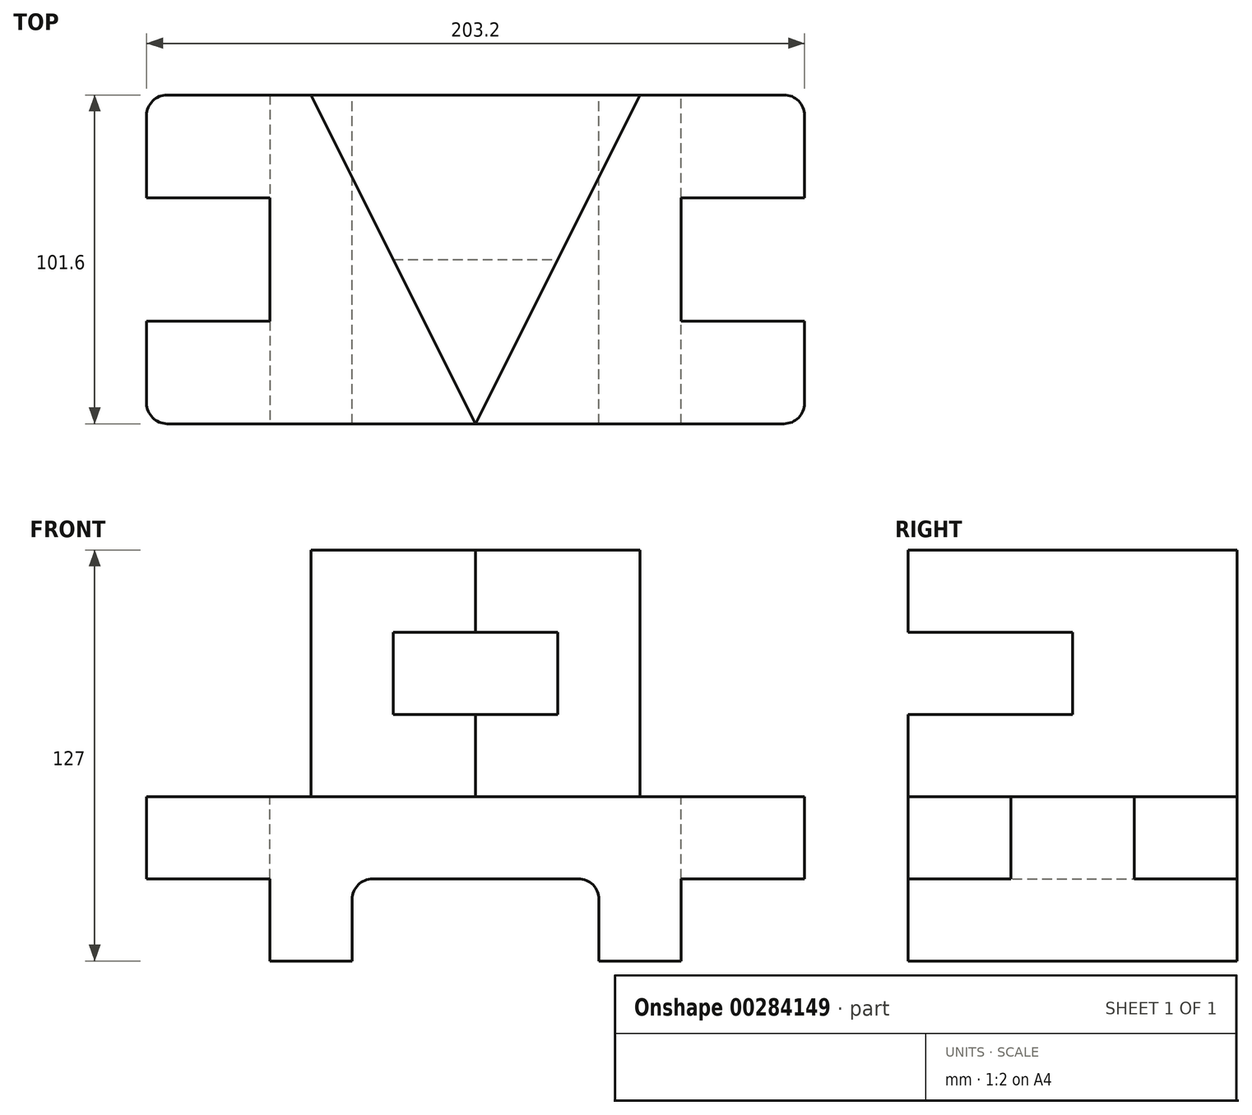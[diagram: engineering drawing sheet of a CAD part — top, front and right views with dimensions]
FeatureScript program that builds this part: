
annotation { "Feature Type Name" : "Feature", "Feature Type Description" : "" }
export const myFeature = defineFeature(function(context is Context, id is Id, definition is map)
    precondition{}
    {
        {
            var Q0;
            Q0=qCreatedBy(makeId("Top.planeOp"),FACE);
            var sketch = newSketch(context, id + "F0", { "sketchPlane" : qUnion([Q0])});
            skLineSegment(sketch, "E0", {"start": v(-63.5, 0) * mm, "end": v(63.5, 0) * mm, "construction": true});
            skLineSegment(sketch, "E1", {"start": v(-63.5, 19.05) * mm, "end": v(-63.5, -19.05) * mm});
            skLineSegment(sketch, "E2", {"start": v(-63.5, -19.05) * mm, "end": v(-101.6, -19.05) * mm});
            skLineSegment(sketch, "E3", {"start": v(-101.6, -19.05) * mm, "end": v(-101.6, -50.8) * mm});
            skLineSegment(sketch, "E4", {"start": v(-101.6, -50.8) * mm, "end": v(101.6, -50.8) * mm});
            skLineSegment(sketch, "E5", {"start": v(101.6, -50.8) * mm, "end": v(101.6, -19.05) * mm});
            skLineSegment(sketch, "E6", {"start": v(101.6, -19.05) * mm, "end": v(63.5, -19.05) * mm});
            skLineSegment(sketch, "E7", {"start": v(63.5, -19.05) * mm, "end": v(63.5, 19.05) * mm});
            skLineSegment(sketch, "E8", {"start": v(63.5, 19.05) * mm, "end": v(101.6, 19.05) * mm});
            skLineSegment(sketch, "E9", {"start": v(101.6, 19.05) * mm, "end": v(101.6, 50.8) * mm});
            skLineSegment(sketch, "E10", {"start": v(101.6, 50.8) * mm, "end": v(-101.6, 50.8) * mm});
            skLineSegment(sketch, "E11", {"start": v(-101.6, 50.8) * mm, "end": v(-101.6, 19.05) * mm});
            skLineSegment(sketch, "E12", {"start": v(-101.6, 19.05) * mm, "end": v(-63.5, 19.05) * mm});
            skSolve(sketch);
        }
        {
            var Q0;
            Q0=makeQuery(id+"F0.imprint","IMPRINT",FACE,{"disambiguationData":[TD([[makeQuery(id+"F0.imprint","IMPRINT",EDGE,{"derivedFrom":sQuery(id+"F0.wireOp",EDGE,"E1")}),1.0]])]});
            extrude(context, id + "F1", {"entities" : qUnion([Q0]), "oppositeDirection" : true, "depth" : 25.4 * mm});
        }
        {
            var Q0;
            Q0=makeQuery(id+"F1.opExtrude","SWEPT_EDGE",EDGE,{"disambiguationData":[OSD([sQuery(id+"F0.wireOp",EDGE,"E3"),sQuery(id+"F0.wireOp",EDGE,"E4")])]});
            var Q1;
            Q1=makeQuery(id+"F1.opExtrude","SWEPT_EDGE",EDGE,{"disambiguationData":[OSD([sQuery(id+"F0.wireOp",EDGE,"E4"),sQuery(id+"F0.wireOp",EDGE,"E5")])]});
            var Q2;
            Q2=makeQuery(id+"F1.opExtrude","SWEPT_EDGE",EDGE,{"disambiguationData":[OSD([sQuery(id+"F0.wireOp",EDGE,"E9"),sQuery(id+"F0.wireOp",EDGE,"E10")])]});
            var Q3;
            Q3=makeQuery(id+"F1.opExtrude","SWEPT_EDGE",EDGE,{"disambiguationData":[OSD([sQuery(id+"F0.wireOp",EDGE,"E10"),sQuery(id+"F0.wireOp",EDGE,"E11")])]});
            fillet(context, id + "F2", {"entities" : qUnion([Q0, Q1, Q2, Q3]), "radius" : 6.35 * mm, "tangentPropagation" : true, "allowEdgeOverflow" : false});
        }
        {
            var Q0;
            Q0=makeQuery(id+"F1.opExtrude","CAP_FACE",FACE,{"disambiguationData":[OSD([sQuery(id+"F0.wireOp",EDGE,"E1"),sQuery(id+"F0.wireOp",EDGE,"E2"),sQuery(id+"F0.wireOp",EDGE,"E3"),sQuery(id+"F0.wireOp",EDGE,"E4"),sQuery(id+"F0.wireOp",EDGE,"E5"),sQuery(id+"F0.wireOp",EDGE,"E6"),sQuery(id+"F0.wireOp",EDGE,"E7"),sQuery(id+"F0.wireOp",EDGE,"E8"),sQuery(id+"F0.wireOp",EDGE,"E9"),sQuery(id+"F0.wireOp",EDGE,"E10"),sQuery(id+"F0.wireOp",EDGE,"E11"),sQuery(id+"F0.wireOp",EDGE,"E12")])],"isStart":false});
            var sketch = newSketch(context, id + "F3", { "sketchPlane" : qUnion([Q0])});
            skLineSegment(sketch, "E13", {"start": v(63.5, 19.05) * mm, "end": v(63.5, 50.8) * mm});
            skLineSegment(sketch, "E14", {"start": v(63.5, 50.8) * mm, "end": v(38.1, 50.8) * mm});
            skLineSegment(sketch, "E15", {"start": v(38.1, 50.8) * mm, "end": v(38.1, -50.8) * mm});
            skLineSegment(sketch, "E16", {"start": v(38.1, -50.8) * mm, "end": v(63.5, -50.8) * mm});
            skLineSegment(sketch, "E17", {"start": v(63.5, -50.8) * mm, "end": v(63.5, -19.05) * mm});
            skLineSegment(sketch, "E18", {"start": v(63.5, -19.05) * mm, "end": v(63.5, 19.05) * mm});
            skLineSegment(sketch, "E19", {"start": v(-63.5, -50.8) * mm, "end": v(-63.5, -19.05) * mm});
            skLineSegment(sketch, "E20", {"start": v(-63.5, -19.05) * mm, "end": v(-63.5, 19.05) * mm});
            skLineSegment(sketch, "E21", {"start": v(-63.5, 19.05) * mm, "end": v(-63.5, 50.8) * mm});
            skLineSegment(sketch, "E22", {"start": v(-63.5, 50.8) * mm, "end": v(-38.1, 50.8) * mm});
            skLineSegment(sketch, "E23", {"start": v(-38.1, 50.8) * mm, "end": v(-38.1, -50.8) * mm});
            skLineSegment(sketch, "E24", {"start": v(-38.1, -50.8) * mm, "end": v(-63.5, -50.8) * mm});
            skSolve(sketch);
        }
        {
            var Q0;
            Q0=makeQuery(id+"F3.imprint","IMPRINT",FACE,{"disambiguationData":[TD([[makeQuery(id+"F3.imprint","IMPRINT",EDGE,{"derivedFrom":sQuery(id+"F3.wireOp",EDGE,"E19")}),-1.0]])]});
            var Q1;
            Q1=makeQuery(id+"F3.imprint","IMPRINT",FACE,{"disambiguationData":[TD([[makeQuery(id+"F3.imprint","IMPRINT",EDGE,{"derivedFrom":sQuery(id+"F3.wireOp",EDGE,"E13")}),1.0]])]});
            extrude(context, id + "F4", {"entities" : qUnion([Q0, Q1]), "operationType" : NewBodyOperationType.ADD, "depth" : 25.4 * mm});
        }
        {
            var Q0;
            Q0=makeQuery(id+"F4.opExtrude","CAP_EDGE",EDGE,{"disambiguationData":[OSD([sQuery(id+"F3.wireOp",EDGE,"E23")])],"isStart":true});
            var Q1;
            Q1=makeQuery(id+"F4.opExtrude","CAP_EDGE",EDGE,{"disambiguationData":[OSD([sQuery(id+"F3.wireOp",EDGE,"E15")])],"isStart":true});
            fillet(context, id + "F5", {"entities" : qUnion([Q0, Q1]), "radius" : 6.35 * mm, "tangentPropagation" : true, "allowEdgeOverflow" : false});
        }
        {
            var Q0;
            Q0=makeQuery(id+"F1.opExtrude","CAP_FACE",FACE,{"disambiguationData":[OSD([sQuery(id+"F0.wireOp",EDGE,"E1"),sQuery(id+"F0.wireOp",EDGE,"E2"),sQuery(id+"F0.wireOp",EDGE,"E3"),sQuery(id+"F0.wireOp",EDGE,"E4"),sQuery(id+"F0.wireOp",EDGE,"E5"),sQuery(id+"F0.wireOp",EDGE,"E6"),sQuery(id+"F0.wireOp",EDGE,"E7"),sQuery(id+"F0.wireOp",EDGE,"E8"),sQuery(id+"F0.wireOp",EDGE,"E9"),sQuery(id+"F0.wireOp",EDGE,"E10"),sQuery(id+"F0.wireOp",EDGE,"E11"),sQuery(id+"F0.wireOp",EDGE,"E12")])],"isStart":true});
            var sketch = newSketch(context, id + "F6", { "sketchPlane" : qUnion([Q0])});
            skLineSegment(sketch, "E25", {"start": v(0, -50.8) * mm, "end": v(-50.8, 50.8) * mm});
            skLineSegment(sketch, "E26", {"start": v(0, -50.8) * mm, "end": v(50.8, 50.8) * mm});
            skLineSegment(sketch, "E27", {"start": v(-50.8, 50.8) * mm, "end": v(50.8, 50.8) * mm});
            skLineSegment(sketch, "E28", {"start": v(0, 0) * mm, "end": v(-25.4, 0) * mm});
            skLineSegment(sketch, "E29", {"start": v(-25.4, 0) * mm, "end": v(25.4, 0) * mm});
            skSolve(sketch);
        }
        {
            var Q0;
            {var subQ4=sQuery(id+"F6.wireOp",EDGE,"E27");Q0=makeQuery(id+"F6.imprint","IMPRINT",FACE,{"disambiguationData":[TD([[makeQuery(id+"F6.imprint","IMPRINT",EDGE,{"derivedFrom":subQ4}),1.0]])]});}
            var Q1;
            {var subQ3=sQuery(id+"F6.wireOp",EDGE,"E29");var subQ5=makeQuery(id+"F6.imprint","IMPRINT",VERTEX,{"derivedFrom":subQ3});Q1=makeQuery(id+"F6.imprint","IMPRINT",FACE,{"disambiguationData":[TD([[makeQuery(id+"F6.imprint","IMPRINT",EDGE,{"disambiguationData":[TD([[subQ5,1.0]])],"derivedFrom":subQ3}),-1.0]])]});}
            extrude(context, id + "F7", {"entities" : qUnion([Q0, Q1]), "operationType" : NewBodyOperationType.ADD, "depth" : 76.2 * mm});
        }
        {
            var Q0;
            {var subQ3=sQuery(id+"F6.wireOp",EDGE,"E29");var subQ5=makeQuery(id+"F6.imprint","IMPRINT",VERTEX,{"derivedFrom":subQ3});Q0=makeQuery(id+"F6.imprint","IMPRINT",FACE,{"disambiguationData":[TD([[makeQuery(id+"F6.imprint","IMPRINT",EDGE,{"disambiguationData":[TD([[subQ5,1.0]])],"derivedFrom":subQ3}),-1.0]])]});}
            extrude(context, id + "F8", {"entities" : qUnion([Q0]), "operationType" : NewBodyOperationType.REMOVE, "depth" : 50.8 * mm, "hasSecondDirection" : true, "secondDirectionOppositeDirection" : false, "secondDirectionDepth" : 25.4 * mm});
        }
    });
